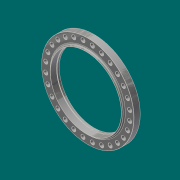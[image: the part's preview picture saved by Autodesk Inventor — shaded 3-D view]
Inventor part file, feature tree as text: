
AUTODESK INVENTOR PART (.ipt)
format: ipt  version: 2017.3 (Build 213257000, 257)  size: 306,688 bytes
history: native  units: in
note: dims shown in document units (in); Inventor stores cm internally (conversion verified against a paired STEP export)
features: sketch x6, extrude x3, chamfer x3, fillet x2, hole x1, pattern_circular x1, plane x1, loft x1, revolve x1, other x1
ambient origin geometry x8: Origin, YZ Plane, XZ Plane, XY Plane, X Axis, Y Axis, Z Axis, Center Point
bodies: Solid1 (feature_tree)
feature tree (20):
  extrude  "Extrusion1"  Depth=3.0in TaperAngle=0.0deg
  hole  "Hole1"  [1 undecoded]
  chamfer  "Chamfer1"  Distance=11.0236in Angle=360.0deg
  pattern_circular  "Circular Pattern1"  [2 undecoded]
  chamfer  "Chamfer2"  Distance=30.0in
  sketch  "Sketch3"  dims[d5=1.875in d6=0.75in d7=0.375in d8=0.25in d9=0.5635in d10=1.0in d11=0.8108in d12=11.0236in d13=360.0deg]
  plane  "Work Plane1"
  extrude  "Extrusion2"  Depth=0.5in TaperAngle=0.0deg
  loft  "Loft1"
  fillet  "Fillet1"  [1 undecoded]
  revolve  "Revolution1"  [1 undecoded]
  extrude  "Extrusion3"  Depth=0.0312in
  chamfer  "Chamfer3"  Distance=0.5in
  fillet  "Fillet2"  Radius=0.4375in
  sketch  "Sketch1"  dims[d0=43.0in d1=3.0in d2=0.0in]
  sketch  "Sketch2"  dims[d3=39.25in d4=0.0442in]
  sketch  "Sketch4"  dims[d15=0.0625in d16=0.125in d17=45.0deg]
  other  "Edges1"
  sketch  "Sketch5"  dims[d18=0.0625in d19=0.125in d20=45.0deg]
  sketch  "Sketch6"  dims[d21=35.25in d22=6.0in d23=30.0in d24=0.5in d25=0.0in d26=0.0in d27=90.0deg d28=0.0in d29=90.0deg d30=0.5in d31=34.0in d32=0.5in d33=0.4375in d34=0.2577in d35=0.5in d36=3.875in d37=0.0393in d38=90.0deg d39=32.5in d40=1.0in d41=0.0in d42=0.0312in d43=0.125in d44=45.0deg d45=0.0312in]
note: 5 required parameter values undecoded (feature->parameter linkage not recoverable at this tier; creation-order binding heuristic only, values carry confidence <= 0.55)